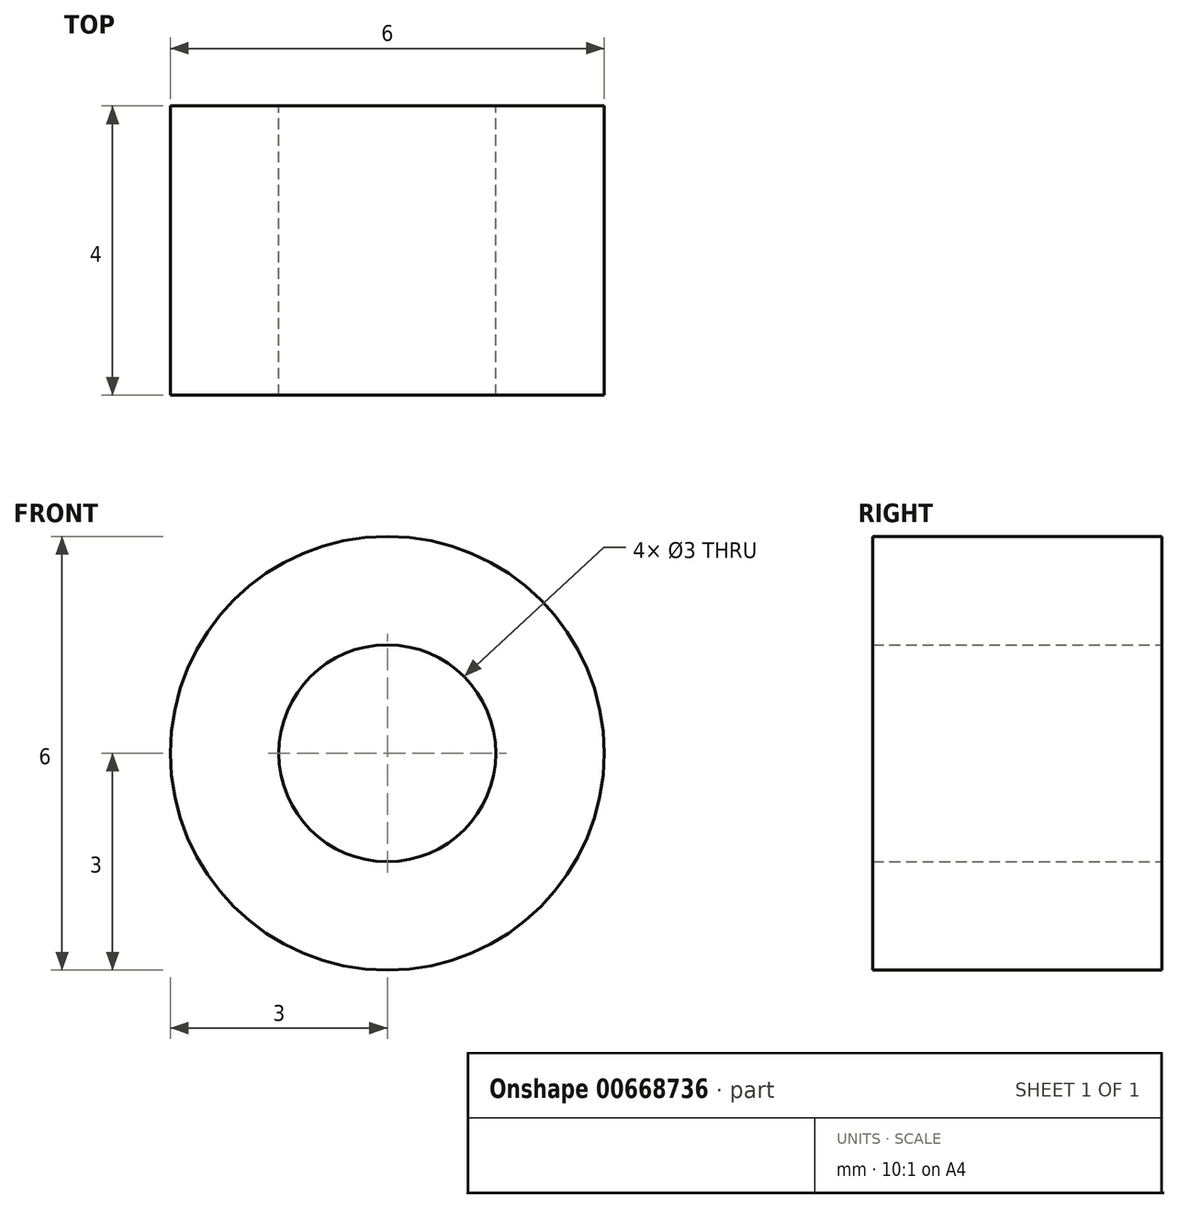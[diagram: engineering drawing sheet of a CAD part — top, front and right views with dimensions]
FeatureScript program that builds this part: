
annotation { "Feature Type Name" : "Feature", "Feature Type Description" : "" }
export const myFeature = defineFeature(function(context is Context, id is Id, definition is map)
    precondition{}
    {
        {
            var Q0;
            Q0=qCreatedBy(makeId("Front.planeOp"),FACE);
            var sketch = newSketch(context, id + "F0", { "sketchPlane" : qUnion([Q0])});
            skCircle(sketch, "E0", {"center": v(0, 0) * mm, "radius": 1.5 * mm});
            skCircle(sketch, "E1", {"center": v(0, 0) * mm, "radius": 3 * mm});
            skSolve(sketch);
        }
        {
            var Q0;
            Q0=makeQuery(id+"F0.imprint","IMPRINT",FACE,{"disambiguationData":[TD([[makeQuery(id+"F0.imprint","IMPRINT",EDGE,{"derivedFrom":sQuery(id+"F0.wireOp",EDGE,"E0")}),-1.0]])]});
            extrude(context, id + "F1", {"entities" : qUnion([Q0]), "depth" : 4 * mm, "offsetDistance" : 25 * mm});
        }
    });
